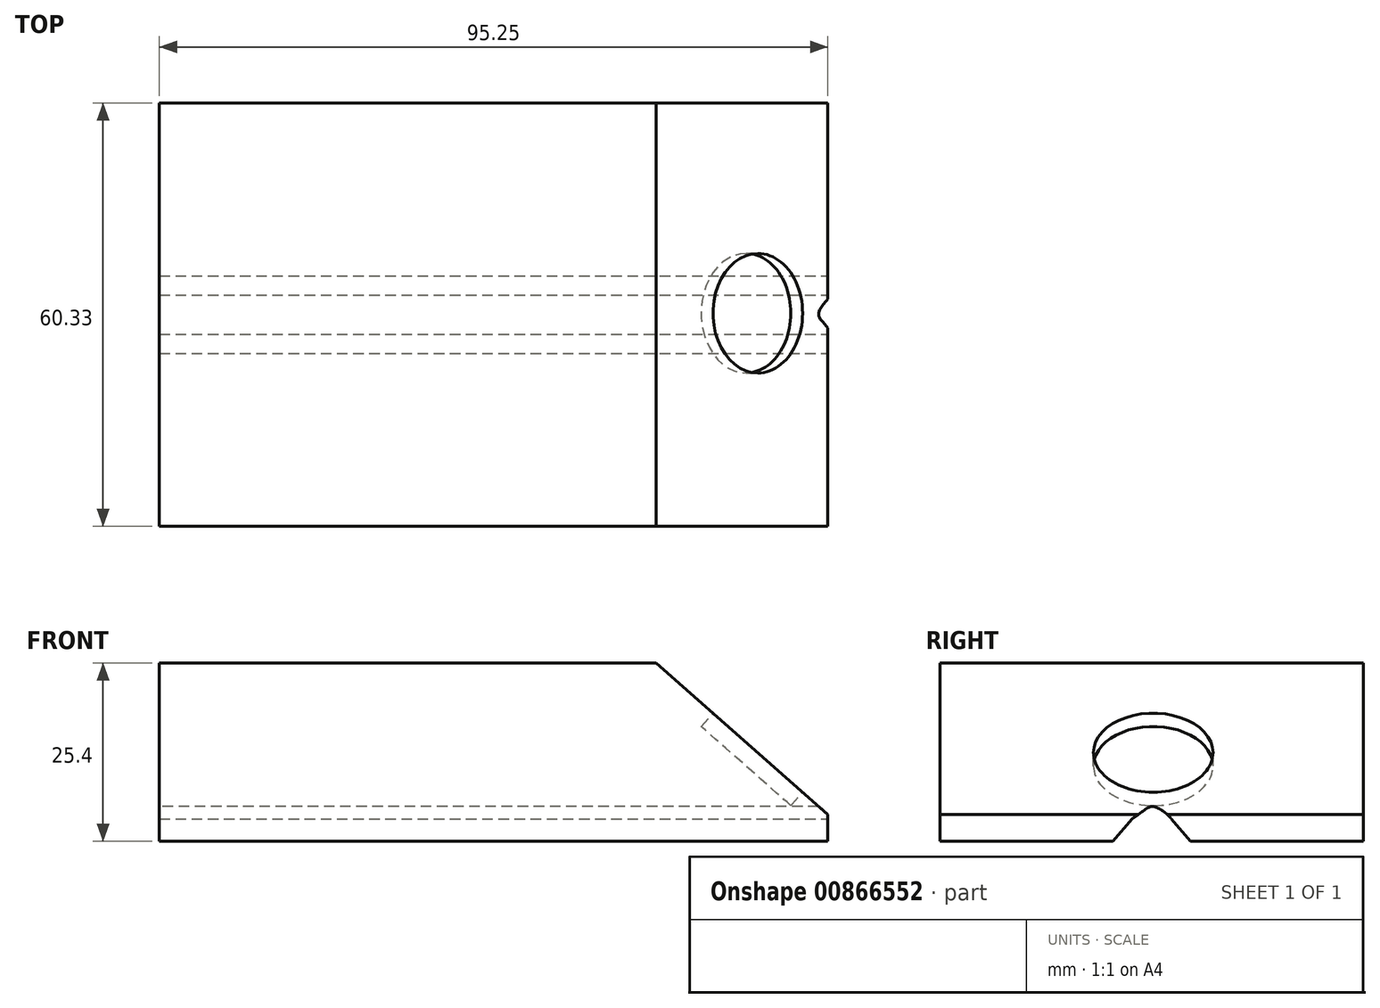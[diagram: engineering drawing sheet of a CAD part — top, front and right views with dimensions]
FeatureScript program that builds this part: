
annotation { "Feature Type Name" : "Feature", "Feature Type Description" : "" }
export const myFeature = defineFeature(function(context is Context, id is Id, definition is map)
    precondition{}
    {
        {
            var Q0;
            Q0=qCreatedBy(makeId("Top.planeOp"),FACE);
            var sketch = newSketch(context, id + "F0", { "sketchPlane" : qUnion([Q0])});
            skLineSegment(sketch, "E0.bottom", {"start": v(-40.69, 15.37) * mm, "end": v(54.56, 15.37) * mm});
            skLineSegment(sketch, "E0.top", {"start": v(-40.69, -44.96) * mm, "end": v(54.56, -44.96) * mm});
            skLineSegment(sketch, "E0.left", {"start": v(-40.69, 15.37) * mm, "end": v(-40.69, -44.96) * mm});
            skLineSegment(sketch, "E0.right", {"start": v(54.56, 15.37) * mm, "end": v(54.56, -44.96) * mm});
            skSolve(sketch);
        }
        {
            var Q0;
            Q0 = qSketchRegion(id + "F0", true);
            extrude(context, id + "F1", {"entities" : qUnion([Q0]), "depth" : 25.4 * mm, "offsetDistance" : 25.4 * mm});
        }
        {
            var Q0;
            Q0=makeQuery(id+"F1.opExtrude","SWEPT_FACE",FACE,{"disambiguationData":[OSD([sQuery(id+"F0.wireOp",EDGE,"E0.right")])]});
            var sketch = newSketch(context, id + "F2", { "sketchPlane" : qUnion([Q0])});
            skLineSegment(sketch, "E1", {"start": v(-20.31, 0) * mm, "end": v(-17.6, 3.21) * mm});
            skLineSegment(sketch, "E2", {"start": v(-12, 3.21) * mm, "end": v(-9.28, 0) * mm});
            skPoint(sketch, "E3.1.internal.snap0", {"position": v(-14.8, 0) * mm});
            skFitSpline(sketch, "E3", {"points": [v(-17.6, 3.21) * mm, v(-14.8, 4.96) * mm, v(-12, 3.21) * mm], "startDerivative": vector(11.2, 7.18) * mm, "endDerivative": vector(7.04, -7.65) * mm});
            skLineSegment(sketch, "E4", {"start": v(-20.31, 0) * mm, "end": v(-14.8, 0) * mm});
            skLineSegment(sketch, "E5", {"start": v(-14.8, 0) * mm, "end": v(-9.28, 0) * mm});
            skSolve(sketch);
        }
        {
            var Q0;
            Q0 = qSketchRegion(id + "F2", true);
            extrude(context, id + "F3", {"entities" : qUnion([Q0]), "operationType" : NewBodyOperationType.REMOVE, "oppositeDirection" : true, "depth" : 95.25 * mm, "offsetDistance" : 25.4 * mm});
        }
        {
            var Q0;
            Q0=makeQuery(id+"F1.opExtrude","SWEPT_FACE",FACE,{"disambiguationData":[OSD([sQuery(id+"F0.wireOp",EDGE,"E0.bottom")])]});
            var sketch = newSketch(context, id + "F4", { "sketchPlane" : qUnion([Q0])});
            skLineSegment(sketch, "E6", {"start": v(-58.88, 0) * mm, "end": v(-23.17, 31.53) * mm});
            skLineSegment(sketch, "E7", {"start": v(-23.17, 31.53) * mm, "end": v(-60.72, 31.53) * mm});
            skLineSegment(sketch, "E8", {"start": v(-60.72, 31.53) * mm, "end": v(-58.88, 0) * mm});
            skSolve(sketch);
        }
        {
            var Q0;
            Q0 = qSketchRegion(id + "F4", true);
            extrude(context, id + "F5", {"entities" : qUnion([Q0]), "operationType" : NewBodyOperationType.REMOVE, "oppositeDirection" : true, "depth" : 95.25 * mm, "offsetDistance" : 25.4 * mm});
        }
        {
            var Q0;
            Q0=makeQuery(id+"F5.boolean.opBoolean","COPY",FACE,{"derivedFrom":makeQuery(id+"F5.opExtrude","SWEPT_FACE",FACE,{"disambiguationData":[OSD([sQuery(id+"F4.wireOp",EDGE,"E6")])]})});
            var sketch = newSketch(context, id + "F6", { "sketchPlane" : qUnion([Q0])});
            skCircle(sketch, "E9", {"center": v(25.07, -14.6) * mm, "radius": 8.52 * mm});
            skSolve(sketch);
        }
        {
            var Q0;
            Q0 = qSketchRegion(id + "F6", true);
            extrude(context, id + "F7", {"entities" : qUnion([Q0]), "operationType" : NewBodyOperationType.REMOVE, "oppositeDirection" : true, "depth" : 2.54 * mm, "offsetDistance" : 25.4 * mm});
        }
    });
